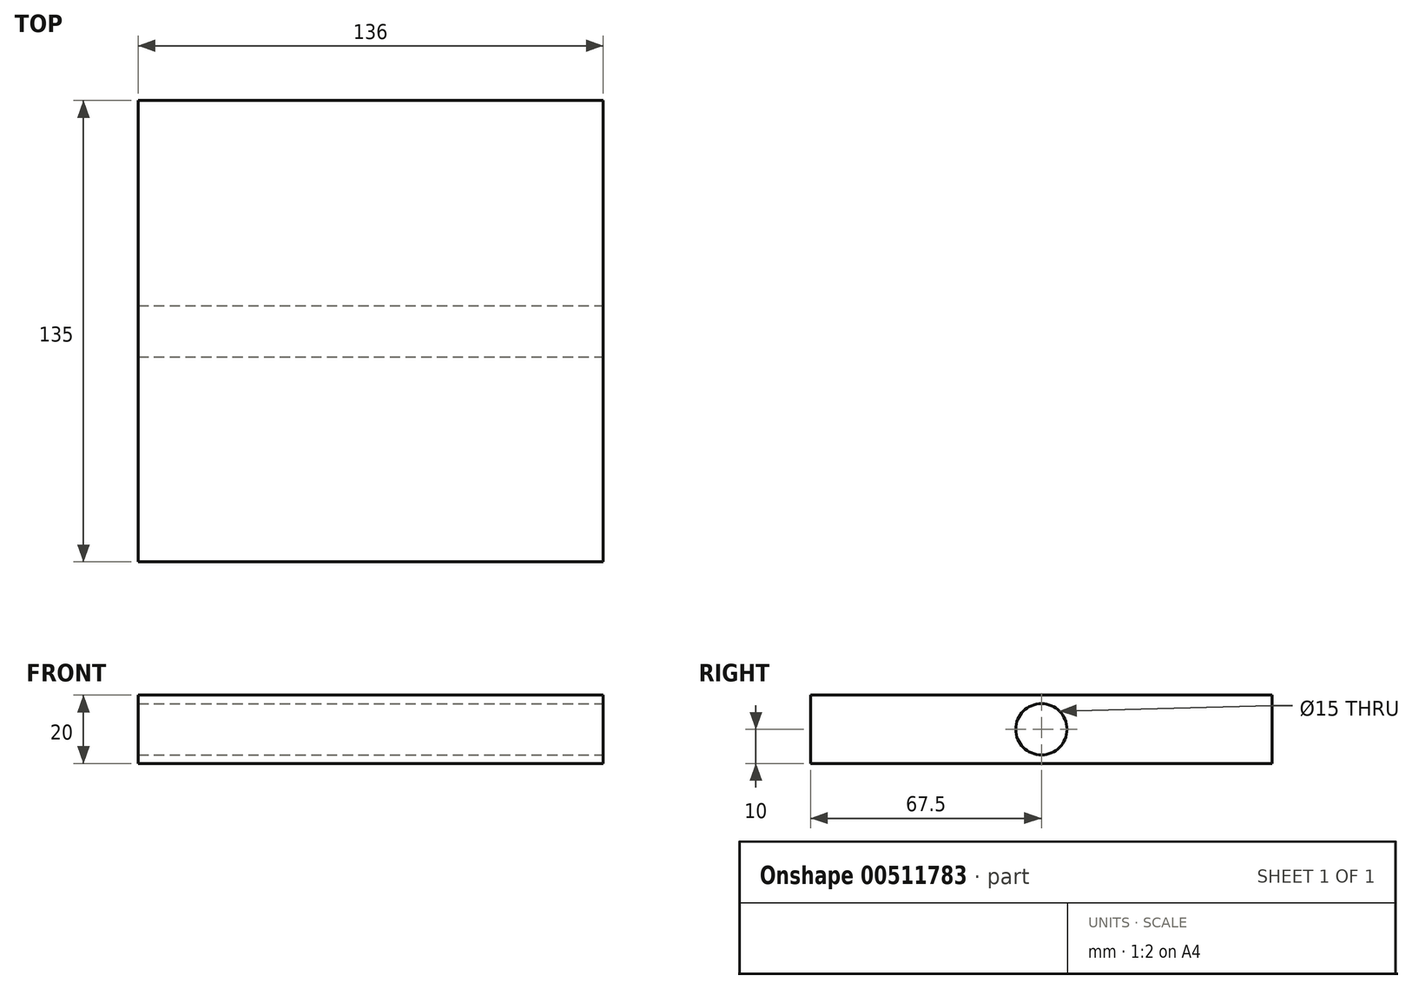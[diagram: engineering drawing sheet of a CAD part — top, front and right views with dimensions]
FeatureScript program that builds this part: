
annotation { "Feature Type Name" : "Feature", "Feature Type Description" : "" }
export const myFeature = defineFeature(function(context is Context, id is Id, definition is map)
    precondition{}
    {
        {
            var Q0;
            Q0=qCreatedBy(makeId("Right.planeOp"),FACE);
            var sketch = newSketch(context, id + "F0", { "sketchPlane" : qUnion([Q0])});
            skLineSegment(sketch, "E0.bottom", {"start": v(67.5, 10) * mm, "end": v(-67.5, 10) * mm});
            skLineSegment(sketch, "E0.top", {"start": v(67.5, -10) * mm, "end": v(-67.5, -10) * mm});
            skLineSegment(sketch, "E0.left", {"start": v(67.5, 10) * mm, "end": v(67.5, -10) * mm});
            skLineSegment(sketch, "E0.right", {"start": v(-67.5, 10) * mm, "end": v(-67.5, -10) * mm});
            skPoint(sketch, "E0.middle", {"position": v(0, 0) * mm});
            skSolve(sketch);
        }
        {
            var Q0;
            Q0=makeQuery(id+"F0.imprint","IMPRINT",FACE,{"disambiguationData":[TD([[makeQuery(id+"F0.imprint","IMPRINT",EDGE,{"derivedFrom":sQuery(id+"F0.wireOp",EDGE,"E0.bottom")}),1.0]])]});
            extrude(context, id + "F1", {"entities" : qUnion([Q0]), "depth" : 136 * mm});
        }
        {
            var Q0;
            Q0=makeQuery(id+"F1.opExtrude","CAP_FACE",FACE,{"disambiguationData":[OSD([sQuery(id+"F0.wireOp",EDGE,"E0.bottom"),sQuery(id+"F0.wireOp",EDGE,"E0.top"),sQuery(id+"F0.wireOp",EDGE,"E0.left"),sQuery(id+"F0.wireOp",EDGE,"E0.right")])],"isStart":false});
            var sketch = newSketch(context, id + "F2", { "sketchPlane" : qUnion([Q0])});
            skCircle(sketch, "E1", {"center": v(0, 0) * mm, "radius": 12.5 * mm});
            skSolve(sketch);
        }
        {
            var Q0;
            Q0=sQuery(id+"F2.wireOp",VERTEX,"E1.center");
            var Q1;
            Q1=makeQuery(id+"F1.opExtrude","SWEPT_BODY",BODY,{"disambiguationData":[OSD([sQuery(id+"F0.wireOp",EDGE,"E0.bottom"),sQuery(id+"F0.wireOp",EDGE,"E0.top"),sQuery(id+"F0.wireOp",EDGE,"E0.left"),sQuery(id+"F0.wireOp",EDGE,"E0.right")])]});
            hole(context, id + "F3", {"style" : HoleStyle.SIMPLE, "endStyle" : HoleEndStyle.THROUGH, "holeDiameter" : 15 * mm, "isTappedThrough" : true, "tappedDepth" : 12 * mm, "tapClearance" : 3, "locations" : qUnion([Q0]), "scope" : qUnion([Q1])});
        }
    });
